# Revit family: Indoor_Pendant Lamp_Santa&Cole_Cirio Lineal
name_source: partatom
category: Luminarias
revit_build: Autodesk Revit 2018 (Build: 20190510_1515(x64)
units: mm (PartAtom-declared; Revit-internal decimal feet)

## family parameters
Compartido = No
Corte con vacíos al cargar = No
Cota de conector redondo = Diámetro de uso
Origen de luz = No
Punto de cálculo de habitación = No
Tipo de pieza = Normal

## types (3) — shared parameters
Assembly Instructions - CE = https://www.santacole.com
Assembly Instructions - UL = https://www.santacole.com
Carga aparente = 0 VA
Energy Label = https://www.santacole.com
Fabricante = Santa & Cole
Manufacturer Website = https://www.santacole.com
Modelo = Cirio Lineal
Technical Information = https://www.santacole.com
URL = https://www.santacole.com
Voltaje (120-277 V) = 220 V

## per-type parameters (varying)
| type | Lampshade Type |
| White Porcelain | Cirio Lampshade : Porcelain Lampshade |
| Brass | Cirio Lampshade : Brass Lampshade |
| White Opal Glass | Cirio Lampshade : White Opal Glass Lampshade |

## geometry (parser evidence)
native form markers: Sweep x5
no freeform markers — native parametric forms only
